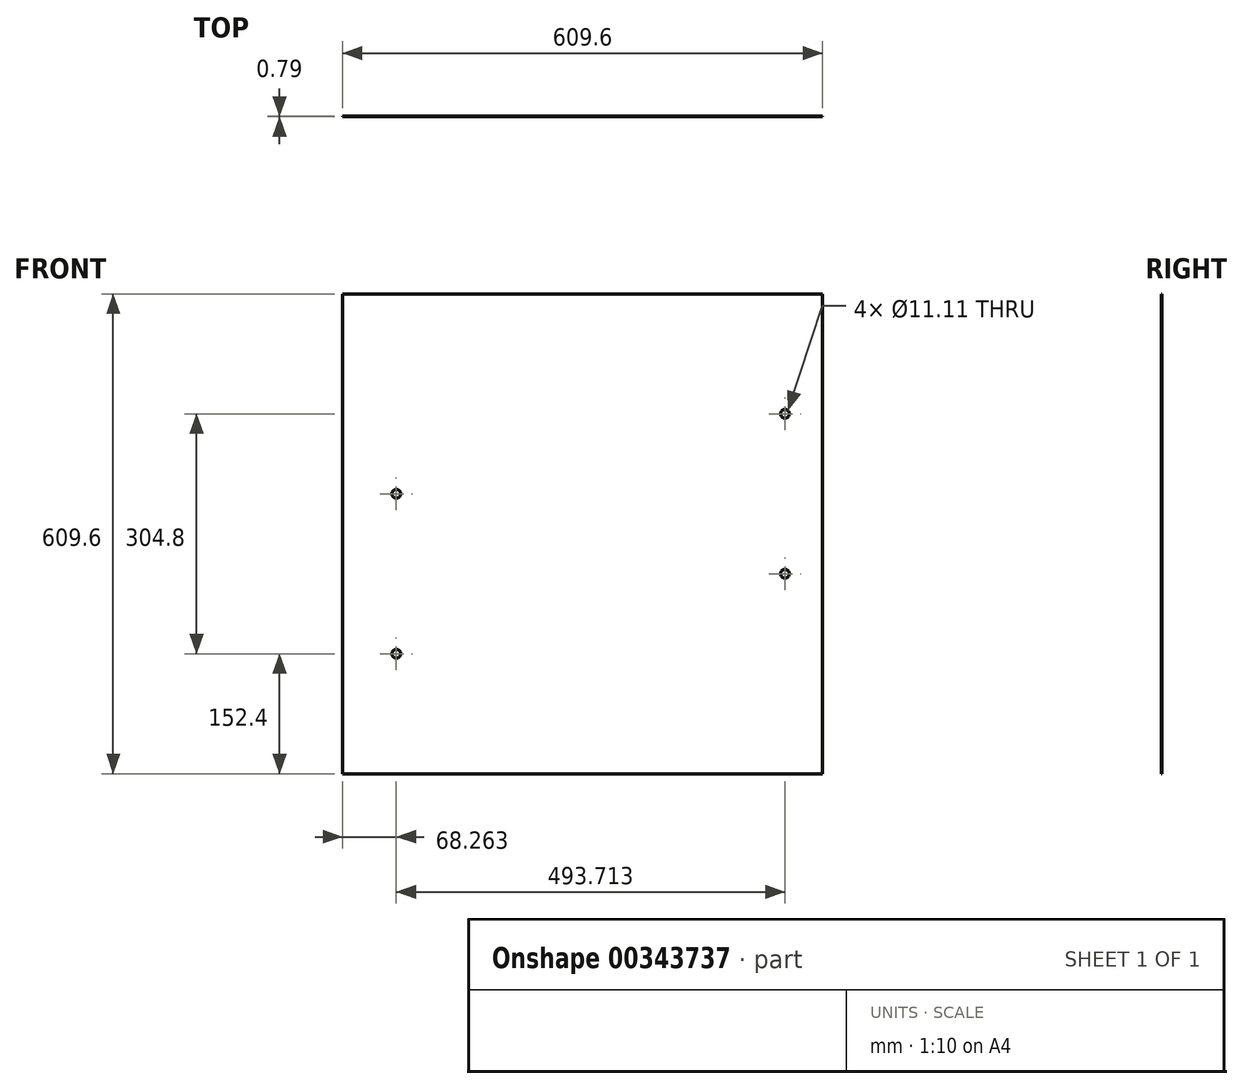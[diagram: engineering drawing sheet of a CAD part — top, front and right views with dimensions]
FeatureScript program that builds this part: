
annotation { "Feature Type Name" : "Feature", "Feature Type Description" : "" }
export const myFeature = defineFeature(function(context is Context, id is Id, definition is map)
    precondition{}
    {
        {
            var Q0;
            Q0=qCreatedBy(makeId("Front.planeOp"),FACE);
            var sketch = newSketch(context, id + "F0", { "sketchPlane" : qUnion([Q0])});
            skLineSegment(sketch, "E0.bottom", {"start": v(0, 0) * mm, "end": v(609.6, 0) * mm});
            skLineSegment(sketch, "E0.top", {"start": v(0, 609.6) * mm, "end": v(609.6, 609.6) * mm});
            skLineSegment(sketch, "E0.left", {"start": v(0, 0) * mm, "end": v(0, 609.6) * mm});
            skLineSegment(sketch, "E0.right", {"start": v(609.6, 0) * mm, "end": v(609.6, 609.6) * mm});
            skSolve(sketch);
        }
        {
            var Q0;
            Q0=makeQuery(id+"F0.imprint","IMPRINT",FACE,{"disambiguationData":[TD([[makeQuery(id+"F0.imprint","IMPRINT",EDGE,{"derivedFrom":sQuery(id+"F0.wireOp",EDGE,"E0.top")}),-1.0]])]});
            extrude(context, id + "F1", {"entities" : qUnion([Q0]), "depth" : 0.8 * mm});
        }
        {
            var Q0;
            Q0=makeQuery(id+"F1.opExtrude","CAP_FACE",FACE,{"disambiguationData":[OSD([sQuery(id+"F0.wireOp",EDGE,"E0.bottom"),sQuery(id+"F0.wireOp",EDGE,"E0.top"),sQuery(id+"F0.wireOp",EDGE,"E0.left"),sQuery(id+"F0.wireOp",EDGE,"E0.right")])],"isStart":false});
            var sketch = newSketch(context, id + "F2", { "sketchPlane" : qUnion([Q0])});
            skCircle(sketch, "E1", {"center": v(68.26, 152.4) * mm, "radius": 5.56 * mm});
            skCircle(sketch, "E2", {"center": v(68.26, 355.6) * mm, "radius": 5.56 * mm});
            skCircle(sketch, "E3", {"center": v(561.97, 457.2) * mm, "radius": 5.56 * mm});
            skCircle(sketch, "E4", {"center": v(561.97, 254) * mm, "radius": 5.56 * mm});
            skSolve(sketch);
        }
        {
            var Q0;
            Q0=makeQuery(id+"F2.imprint","IMPRINT",FACE,{"disambiguationData":[TD([[makeQuery(id+"F2.imprint","IMPRINT",EDGE,{"derivedFrom":sQuery(id+"F2.wireOp",EDGE,"E2")}),1.0]])]});
            var Q1;
            Q1=makeQuery(id+"F2.imprint","IMPRINT",FACE,{"disambiguationData":[TD([[makeQuery(id+"F2.imprint","IMPRINT",EDGE,{"derivedFrom":sQuery(id+"F2.wireOp",EDGE,"E1")}),1.0]])]});
            var Q2;
            Q2=makeQuery(id+"F2.imprint","IMPRINT",FACE,{"disambiguationData":[TD([[makeQuery(id+"F2.imprint","IMPRINT",EDGE,{"derivedFrom":sQuery(id+"F2.wireOp",EDGE,"E4")}),1.0]])]});
            var Q3;
            Q3=makeQuery(id+"F2.imprint","IMPRINT",FACE,{"disambiguationData":[TD([[makeQuery(id+"F2.imprint","IMPRINT",EDGE,{"derivedFrom":sQuery(id+"F2.wireOp",EDGE,"E3")}),1.0]])]});
            extrude(context, id + "F3", {"entities" : qUnion([Q0, Q1, Q2, Q3]), "operationType" : NewBodyOperationType.REMOVE, "oppositeDirection" : true, "depth" : 25.4 * mm});
        }
    });
